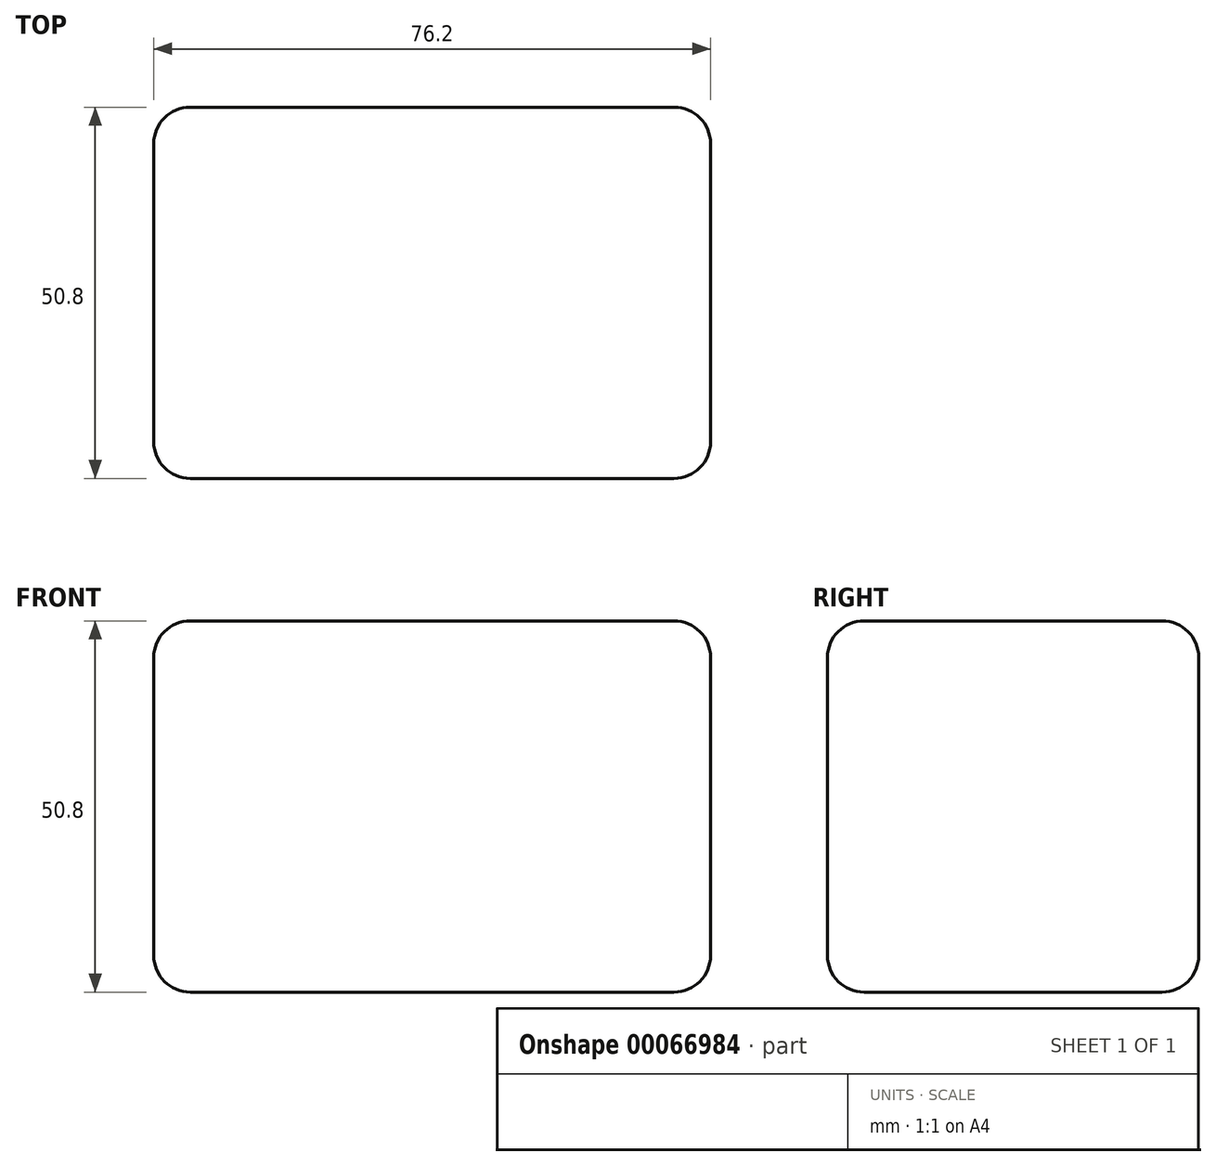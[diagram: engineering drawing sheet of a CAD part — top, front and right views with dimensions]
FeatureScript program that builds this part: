
annotation { "Feature Type Name" : "Feature", "Feature Type Description" : "" }
export const myFeature = defineFeature(function(context is Context, id is Id, definition is map)
    precondition{}
    {
        {
            var Q0;
            Q0=qCreatedBy(makeId("Front.planeOp"),FACE);
            var sketch = newSketch(context, id + "F0", { "sketchPlane" : qUnion([Q0])});
            skLineSegment(sketch, "E0.rect.bottom", {"start": v(38.1, -25.4) * mm, "end": v(-38.1, -25.4) * mm});
            skLineSegment(sketch, "E0.rect.top", {"start": v(38.1, 25.4) * mm, "end": v(-38.1, 25.4) * mm});
            skLineSegment(sketch, "E0.rect.left", {"start": v(38.1, -25.4) * mm, "end": v(38.1, 25.4) * mm});
            skLineSegment(sketch, "E0.rect.right", {"start": v(-38.1, -25.4) * mm, "end": v(-38.1, 25.4) * mm});
            skPoint(sketch, "E0.rect.middle", {"position": v(0, 0) * mm});
            skLineSegment(sketch, "E1", {"start": v(0, 44.41) * mm, "end": v(0, -47.58) * mm, "construction": true});
            skSolve(sketch);
        }
        {
            var Q0;
            Q0=makeQuery(id+"F0.imprint","IMPRINT",FACE,{"disambiguationData":[TD([[makeQuery(id+"F0.imprint","IMPRINT",EDGE,{"derivedFrom":sQuery(id+"F0.wireOp",EDGE,"E0.rect.bottom")}),-1.0]])]});
            extrude(context, id + "F1", {"entities" : qUnion([Q0]), "endBound" : BoundingType.SYMMETRIC, "depth" : 50.8 * mm});
        }
        {
            var Q0;
            Q0=makeQuery(id+"F1.opExtrude","CAP_EDGE",EDGE,{"disambiguationData":[OSD([sQuery(id+"F0.wireOp",EDGE,"E0.rect.top")])],"isStart":false});
            var Q1;
            Q1=makeQuery(id+"F1.opExtrude","SWEPT_EDGE",EDGE,{"disambiguationData":[OSD([sQuery(id+"F0.wireOp",EDGE,"E0.rect.top"),sQuery(id+"F0.wireOp",EDGE,"E0.rect.left")])]});
            var Q2;
            Q2=makeQuery(id+"F1.opExtrude","CAP_EDGE",EDGE,{"disambiguationData":[OSD([sQuery(id+"F0.wireOp",EDGE,"E0.rect.left")])],"isStart":false});
            var Q3;
            Q3=makeQuery(id+"F1.opExtrude","CAP_EDGE",EDGE,{"disambiguationData":[OSD([sQuery(id+"F0.wireOp",EDGE,"E0.rect.right")])],"isStart":false});
            var Q4;
            Q4=makeQuery(id+"F1.opExtrude","SWEPT_EDGE",EDGE,{"disambiguationData":[OSD([sQuery(id+"F0.wireOp",EDGE,"E0.rect.top"),sQuery(id+"F0.wireOp",EDGE,"E0.rect.right")])]});
            var Q5;
            Q5=makeQuery(id+"F1.opExtrude","SWEPT_EDGE",EDGE,{"disambiguationData":[OSD([sQuery(id+"F0.wireOp",EDGE,"E0.rect.bottom"),sQuery(id+"F0.wireOp",EDGE,"E0.rect.right")])]});
            var Q6;
            Q6=makeQuery(id+"F1.opExtrude","CAP_EDGE",EDGE,{"disambiguationData":[OSD([sQuery(id+"F0.wireOp",EDGE,"E0.rect.bottom")])],"isStart":false});
            var Q7;
            Q7=makeQuery(id+"F1.opExtrude","SWEPT_EDGE",EDGE,{"disambiguationData":[OSD([sQuery(id+"F0.wireOp",EDGE,"E0.rect.bottom"),sQuery(id+"F0.wireOp",EDGE,"E0.rect.left")])]});
            var Q8;
            Q8=makeQuery(id+"F1.opExtrude","CAP_EDGE",EDGE,{"disambiguationData":[OSD([sQuery(id+"F0.wireOp",EDGE,"E0.rect.left")])],"isStart":true});
            var Q9;
            Q9=makeQuery(id+"F1.opExtrude","CAP_EDGE",EDGE,{"disambiguationData":[OSD([sQuery(id+"F0.wireOp",EDGE,"E0.rect.top")])],"isStart":true});
            var Q10;
            Q10=makeQuery(id+"F1.opExtrude","CAP_EDGE",EDGE,{"disambiguationData":[OSD([sQuery(id+"F0.wireOp",EDGE,"E0.rect.right")])],"isStart":true});
            var Q11;
            Q11=makeQuery(id+"F1.opExtrude","CAP_EDGE",EDGE,{"disambiguationData":[OSD([sQuery(id+"F0.wireOp",EDGE,"E0.rect.bottom")])],"isStart":true});
            fillet(context, id + "F2", {"entities" : qUnion([Q0, Q1, Q2, Q3, Q4, Q5, Q6, Q7, Q8, Q9, Q10, Q11]), "radius" : 5 * mm, "tangentPropagation" : true, "allowEdgeOverflow" : false});
        }
    });
